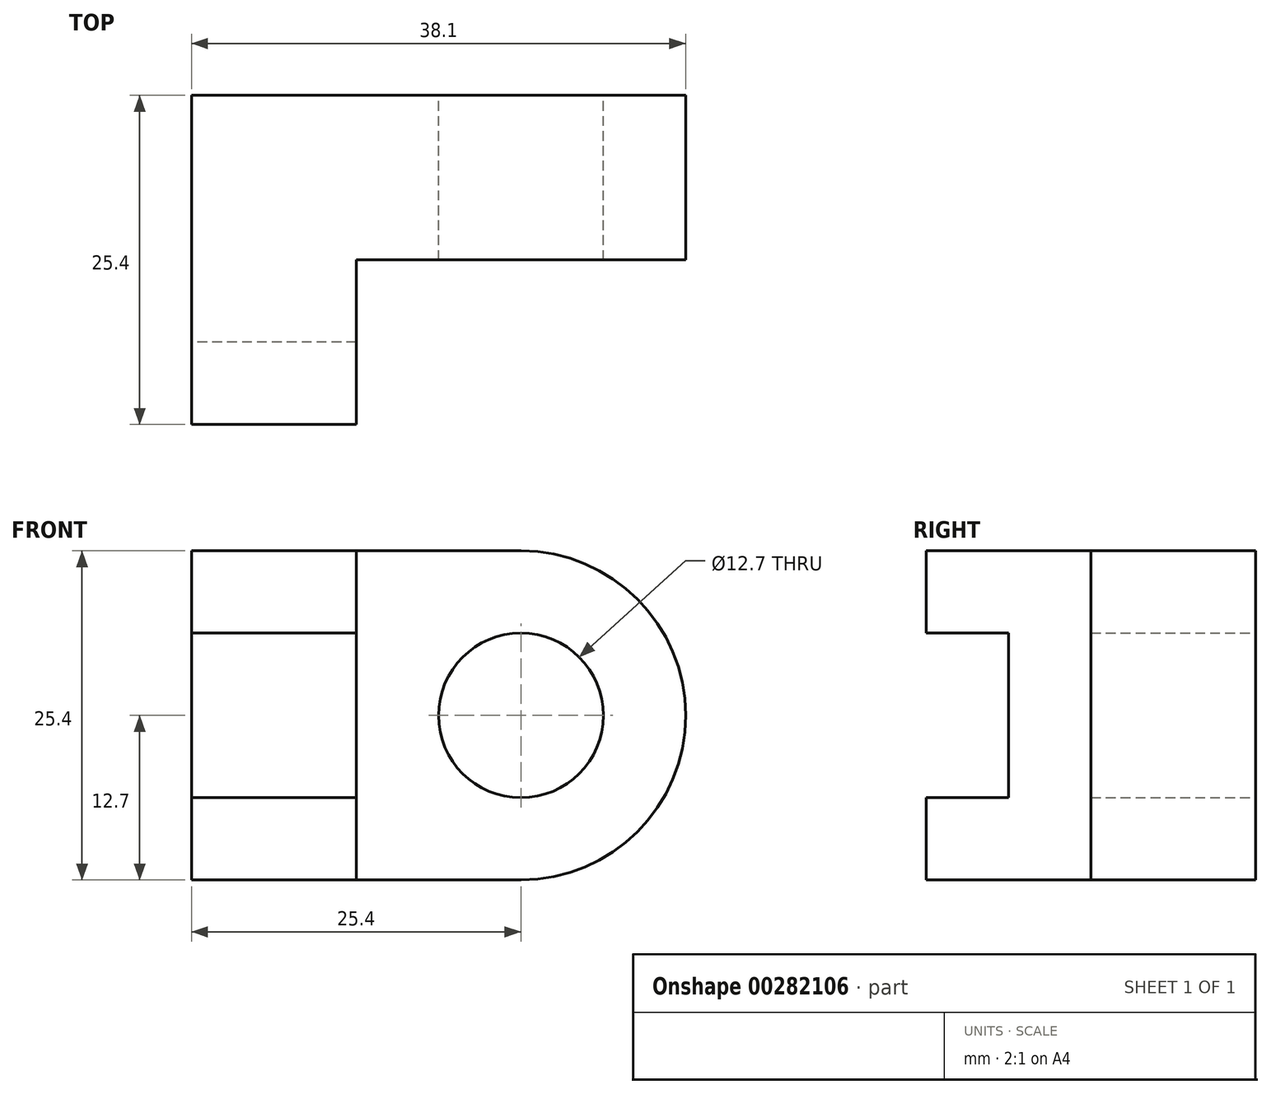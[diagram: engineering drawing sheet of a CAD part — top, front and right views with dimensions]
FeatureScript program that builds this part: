
annotation { "Feature Type Name" : "Feature", "Feature Type Description" : "" }
export const myFeature = defineFeature(function(context is Context, id is Id, definition is map)
    precondition{}
    {
        {
            var Q0;
            Q0=qCreatedBy(makeId("Right.planeOp"),FACE);
            var sketch = newSketch(context, id + "F0", { "sketchPlane" : qUnion([Q0])});
            skLineSegment(sketch, "E0", {"start": v(0, 0) * mm, "end": v(0, 25.4) * mm});
            skLineSegment(sketch, "E1", {"start": v(0, 25.4) * mm, "end": v(-25.4, 25.4) * mm});
            skLineSegment(sketch, "E2", {"start": v(-25.4, 25.4) * mm, "end": v(-25.4, 19.05) * mm});
            skLineSegment(sketch, "E3", {"start": v(-25.4, 19.05) * mm, "end": v(-19.05, 19.05) * mm});
            skLineSegment(sketch, "E4", {"start": v(-19.05, 19.05) * mm, "end": v(-19.05, 6.35) * mm});
            skLineSegment(sketch, "E5", {"start": v(-19.05, 6.35) * mm, "end": v(-25.4, 6.35) * mm});
            skLineSegment(sketch, "E6", {"start": v(-25.4, 6.35) * mm, "end": v(-25.4, 0) * mm});
            skLineSegment(sketch, "E7", {"start": v(-25.4, 0) * mm, "end": v(0, 0) * mm});
            skSolve(sketch);
        }
        {
            var Q0;
            Q0 = qSketchRegion(id + "F0", true);
            extrude(context, id + "F1", {"entities" : qUnion([Q0]), "depth" : 12.7 * mm});
        }
        {
            var Q0;
            Q0=qCreatedBy(makeId("Front.planeOp"),FACE);
            var sketch = newSketch(context, id + "F2", { "sketchPlane" : qUnion([Q0])});
            skLineSegment(sketch, "E8", {"start": v(12.7, 25.4) * mm, "end": v(25.4, 25.4) * mm});
            skLineSegment(sketch, "E9", {"start": v(12.7, 0) * mm, "end": v(25.4, 0) * mm});
            skArc(sketch, "E10", {"start": v(25.4, 0) * mm, "mid": v(38.1, 12.7) * mm, "end": v(25.4, 25.4) * mm});
            skCircle(sketch, "E11", {"center": v(25.4, 12.7) * mm, "radius": 6.35 * mm});
            skLineSegment(sketch, "E12", {"start": v(12.7, 25.4) * mm, "end": v(12.7, 0) * mm});
            skSolve(sketch);
        }
        {
            var Q0;
            Q0=makeQuery(id+"F2.imprint","IMPRINT",FACE,{"disambiguationData":[TD([[makeQuery(id+"F2.imprint","IMPRINT",EDGE,{"derivedFrom":sQuery(id+"F2.wireOp",EDGE,"E8")}),-1.0]])]});
            extrude(context, id + "F3", {"entities" : qUnion([Q0]), "operationType" : NewBodyOperationType.ADD, "depth" : 12.7 * mm});
        }
    });
